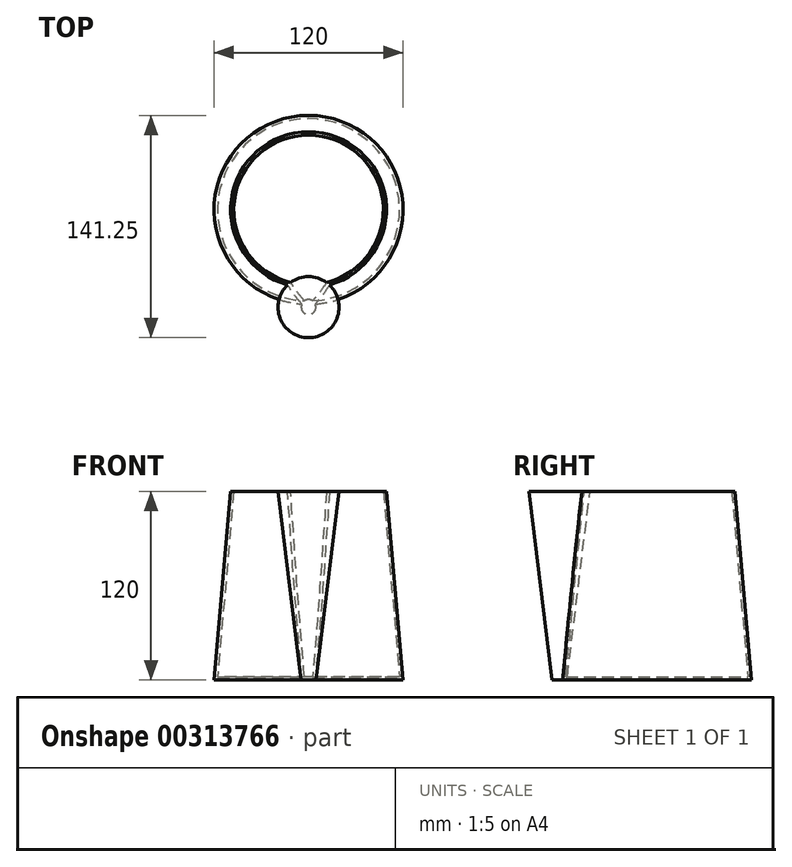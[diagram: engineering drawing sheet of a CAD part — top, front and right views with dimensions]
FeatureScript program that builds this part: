
annotation { "Feature Type Name" : "Feature", "Feature Type Description" : "" }
export const myFeature = defineFeature(function(context is Context, id is Id, definition is map)
    precondition{}
    {
        {
            var Q0;
            Q0=qCreatedBy(makeId("Top.planeOp"),FACE);
            var sketch = newSketch(context, id + "F0", { "sketchPlane" : qUnion([Q0])});
            skCircle(sketch, "E0", {"center": v(0, 0) * mm, "radius": 60 * mm});
            skSolve(sketch);
        }
        {
            var Q0;
            Q0=makeQuery(id+"F0.imprint","IMPRINT",FACE,{"disambiguationData":[TD([[makeQuery(id+"F0.imprint","IMPRINT",EDGE,{"derivedFrom":sQuery(id+"F0.wireOp",EDGE,"E0")}),1.0]])]});
            extrude(context, id + "F1", {"entities" : qUnion([Q0]), "depth" : 120 * mm, "hasDraft" : true, "draftAngle" : 5 * degree, "draftPullDirection" : true});
        }
        {
            var Q0;
            Q0=makeQuery(id+"F1.opExtrude","CAP_FACE",FACE,{"disambiguationData":[OSD([sQuery(id+"F0.wireOp",EDGE,"E0")])],"isStart":false});
            shell(context, id + "F2", {"entities" : qUnion([Q0]), "thickness" : 2 * mm});
        }
        {
            var Q0;
            Q0=makeQuery(id+"F1.opExtrude","CAP_FACE",FACE,{"disambiguationData":[OSD([sQuery(id+"F0.wireOp",EDGE,"E0")])],"isStart":false});
            cPlane(context, id + "F3", {"entities" : qUnion([Q0]), "cplaneType" : CPlaneType.OFFSET, "offset" : 0 * mm, "width" : 150 * mm, "height" : 150 * mm});
        }
        {
            var Q0;
            Q0=qCreatedBy(id+"F3.planeOp",FACE);
            var sketch = newSketch(context, id + "F4", { "sketchPlane" : qUnion([Q0])});
            skCircle(sketch, "E1", {"center": v(0, -61.86) * mm, "radius": 19.39 * mm});
            skSolve(sketch);
        }
        {
            var Q0;
            Q0=makeQuery(id+"F4.imprint","IMPRINT",FACE,{"disambiguationData":[TD([[makeQuery(id+"F4.imprint","IMPRINT",EDGE,{"derivedFrom":sQuery(id+"F4.wireOp",EDGE,"E1")}),1.0]])]});
            var Q1;
            Q1=makeQuery(id+"F1.opExtrude","CAP_FACE",FACE,{"disambiguationData":[OSD([sQuery(id+"F0.wireOp",EDGE,"E0")])],"isStart":true});
            extrude(context, id + "F5", {"entities" : qUnion([Q0]), "operationType" : NewBodyOperationType.ADD, "endBound" : BoundingType.UP_TO_SURFACE, "oppositeDirection" : true, "endBoundEntityFace" : qUnion([Q1]), "depth" : 25 * mm, "hasDraft" : true, "draftAngle" : 7 * degree, "draftPullDirection" : true});
        }
    });
